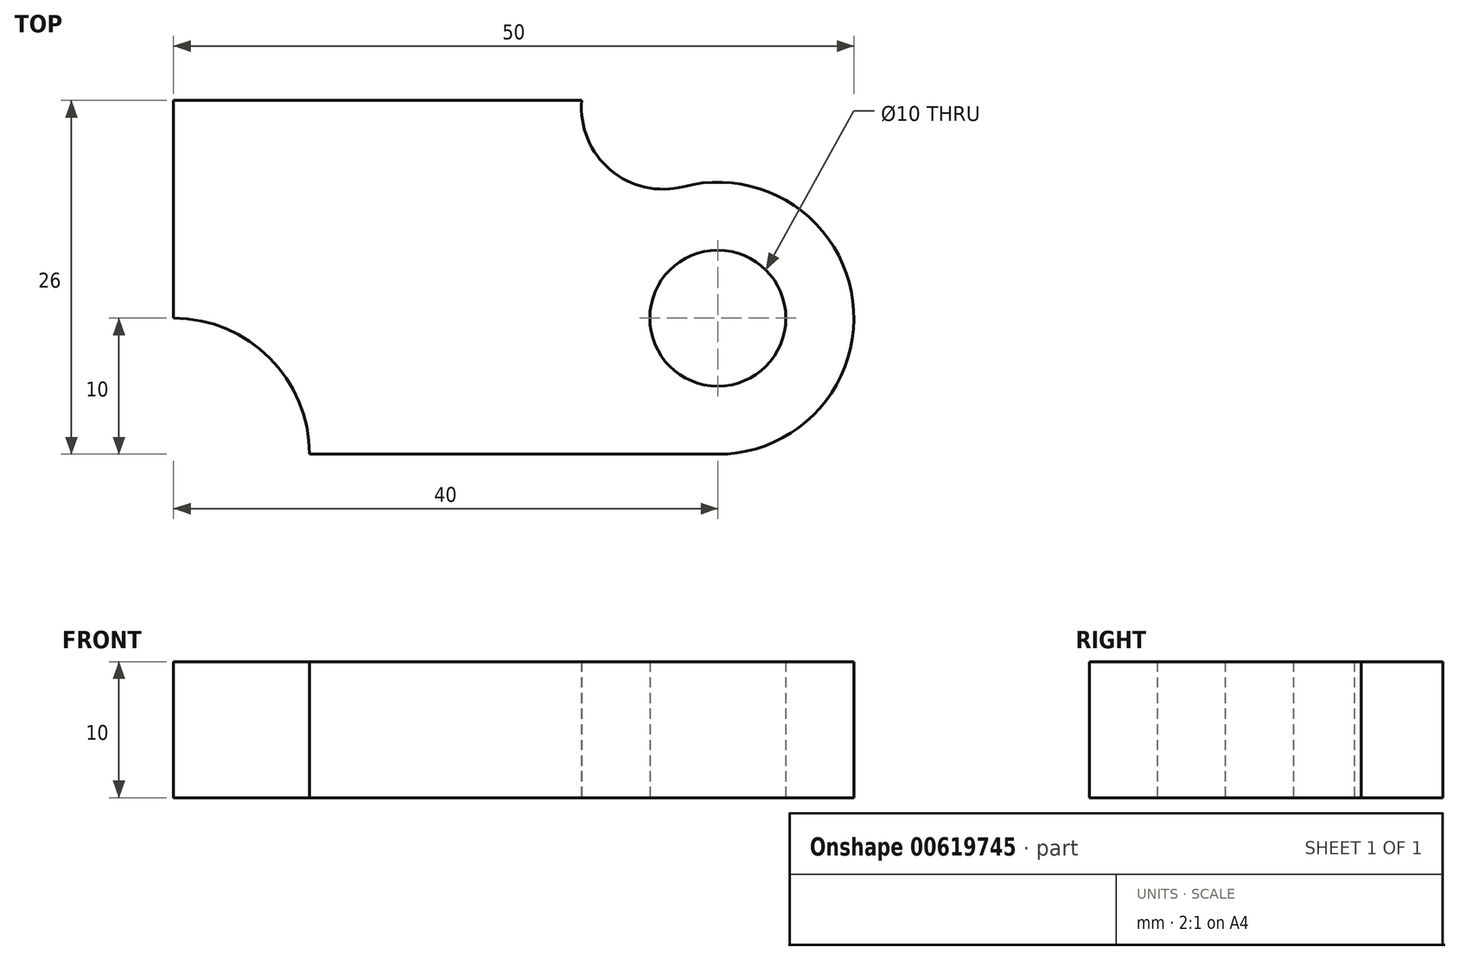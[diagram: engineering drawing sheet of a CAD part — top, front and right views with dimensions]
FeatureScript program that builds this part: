
annotation { "Feature Type Name" : "Feature", "Feature Type Description" : "" }
export const myFeature = defineFeature(function(context is Context, id is Id, definition is map)
    precondition{}
    {
        {
            var Q0;
            Q0=qCreatedBy(makeId("Top.planeOp"),FACE);
            var sketch = newSketch(context, id + "F0", { "sketchPlane" : qUnion([Q0])});
            skLineSegment(sketch, "E0.bottom", {"start": v(-10, -10) * mm, "end": v(-30, -10) * mm});
            skLineSegment(sketch, "E0.top", {"start": v(-10, 16) * mm, "end": v(-40, 16) * mm});
            skLineSegment(sketch, "E0.right", {"start": v(-40, 0) * mm, "end": v(-40, 16) * mm});
            skPoint(sketch, "E0.middle", {"position": v(-25, 3) * mm});
            skArc(sketch, "E1", {"start": v(0, -10) * mm, "mid": v(9.92, 1.27) * mm, "end": v(-2.51, 9.68) * mm});
            skArc(sketch, "E2", {"start": v(-10, 16) * mm, "mid": v(-7.9, 10.9) * mm, "end": v(-2.51, 9.68) * mm});
            skArc(sketch, "E3", {"start": v(-30, -10) * mm, "mid": v(-32.93, -2.93) * mm, "end": v(-40, 0) * mm});
            skLineSegment(sketch, "E4", {"start": v(-10, -10) * mm, "end": v(0, -10) * mm});
            skCircle(sketch, "E5", {"center": v(0, 0) * mm, "radius": 5 * mm});
            skSolve(sketch);
        }
        {
            var Q0;
            Q0=makeQuery(id+"F0.imprint","IMPRINT",FACE,{"disambiguationData":[TD([[makeQuery(id+"F0.imprint","IMPRINT",EDGE,{"derivedFrom":sQuery(id+"F0.wireOp",EDGE,"E0.bottom")}),-1.0]])]});
            extrude(context, id + "F1", {"entities" : qUnion([Q0]), "depth" : 10 * mm, "offsetDistance" : 25 * mm});
        }
    });
